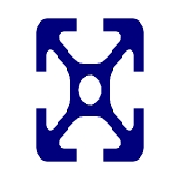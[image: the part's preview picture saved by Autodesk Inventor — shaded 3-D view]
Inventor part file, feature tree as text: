
AUTODESK INVENTOR PART (.ipt)
format: ipt  version: 2020 (Build 240168000, 168)  size: 273,920 bytes
history: native  units: mm
features: other x16, sketch x8
ambient origin geometry x8: Origin, YZ Plane, XZ Plane, XY Plane, X Axis, Y Axis, Z Axis, Center Point
bodies: Body (feature_tree)
feature tree (24):
  other  "Řízená délka"
  other  "Těleso1"
  other  "Start Plane"
  other  "End Plane"
  other  "iFeatureSketch"
  other  "DRAZKA_20:1"
  other  "DRAZKA_20:2"
  other  "DRAZKA_20:3"
  other  "DRAZKA_20:4"
  other  "DIRA_20:1"
  other  "DRAZKA_20:1Axis"
  other  "DRAZKA_20:2Axis"
  other  "DRAZKA_20:3Axis"
  other  "DRAZKA_20:4Axis"
  other  "DIRA_20:1Axis"
  sketch  "Sketch"  dims[d2=20.0mm d3=20.0mm d4=2.0mm d9=-0.0mm d10=420.0mm d11=0.13mm d12=0.0mm d15=0.83mm d16=0.83mm d17=9.8mm d18=3.0mm d19=4.55mm d20=45.0deg d21=5.2mm d22=1.8mm d24=1.0mm d26=0.83mm d27=0.83mm d28=9.8mm d29=3.0mm d30=4.55mm d31=45.0deg d32=5.2mm d33=1.8mm d35=1.0mm d37=0.83mm d38=0.83mm d39=9.8mm d40=3.0mm d41=4.55mm d42=45.0deg d43=5.2mm d44=1.8mm d46=1.0mm d48=0.83mm d49=0.83mm d50=9.8mm d51=3.0mm d52=4.55mm d53=45.0deg d54=5.2mm d55=1.8mm d57=1.0mm d59=4.3mm d60=0.0mm d61=0.0mm d62=0.0mm d63=0.0mm d64=0.0mm d65=0.0mm d66=0.0mm d67=0.0mm d76=90.0deg d14=420.0mm]
  sketch  "Náčrt11"
  other  "Pracovní rovina4"
  sketch  "Náčrt12"
  sketch  "Náčrt6"
  sketch  "Náčrt7"
  sketch  "Náčrt8"
  sketch  "Náčrt9"
  sketch  "Náčrt10"
